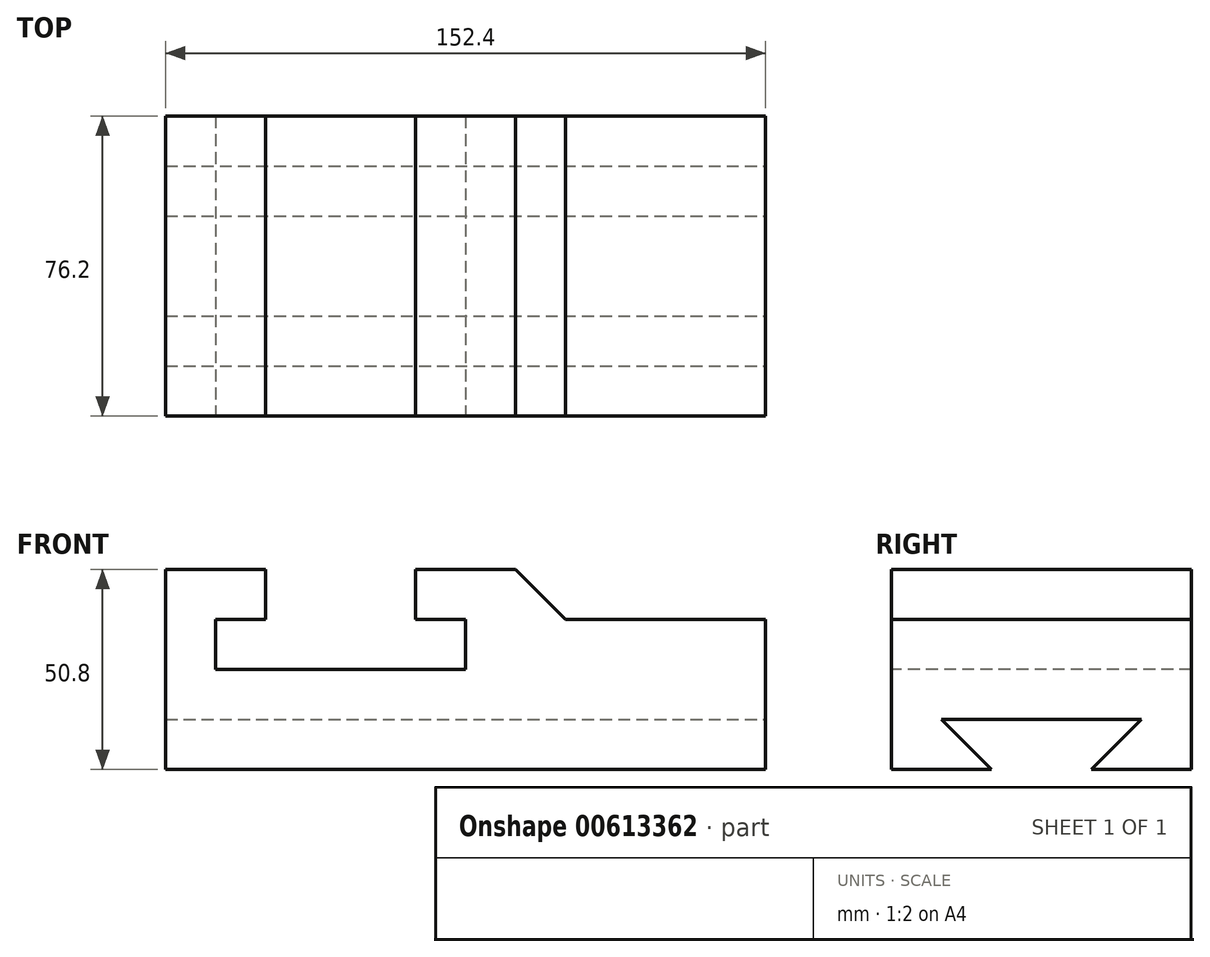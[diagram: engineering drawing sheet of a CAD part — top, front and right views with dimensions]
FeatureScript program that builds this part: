
annotation { "Feature Type Name" : "Feature", "Feature Type Description" : "" }
export const myFeature = defineFeature(function(context is Context, id is Id, definition is map)
    precondition{}
    {
        {
            var Q0;
            Q0=qCreatedBy(makeId("Front.planeOp"),FACE);
            var sketch = newSketch(context, id + "F0", { "sketchPlane" : qUnion([Q0])});
            skLineSegment(sketch, "E0", {"start": v(0, 0) * mm, "end": v(0, -50.8) * mm});
            skLineSegment(sketch, "E1", {"start": v(0, 0) * mm, "end": v(152.4, 0) * mm});
            skLineSegment(sketch, "E2", {"start": v(0, -50.8) * mm, "end": v(152.4, -50.8) * mm});
            skLineSegment(sketch, "E3", {"start": v(152.4, -50.8) * mm, "end": v(152.4, 0) * mm});
            skSolve(sketch);
        }
        {
            var Q0;
            Q0 = qSketchRegion(id + "F0", true);
            extrude(context, id + "F1", {"entities" : qUnion([Q0]), "depth" : 76.2 * mm, "offsetDistance" : 25.4 * mm});
        }
        {
            var Q0;
            Q0=makeQuery(id+"F1.opExtrude","CAP_FACE",FACE,{"disambiguationData":[OSD([sQuery(id+"F0.wireOp",EDGE,"E0"),sQuery(id+"F0.wireOp",EDGE,"E1"),sQuery(id+"F0.wireOp",EDGE,"E2"),sQuery(id+"F0.wireOp",EDGE,"E3")])],"isStart":false});
            var sketch = newSketch(context, id + "F2", { "sketchPlane" : qUnion([Q0])});
            skLineSegment(sketch, "E4", {"start": v(152.4, 0) * mm, "end": v(88.9, 0) * mm});
            skLineSegment(sketch, "E5", {"start": v(152.4, -12.7) * mm, "end": v(152.4, 0) * mm});
            skLineSegment(sketch, "E6", {"start": v(88.9, 0) * mm, "end": v(101.6, -12.7) * mm});
            skLineSegment(sketch, "E7", {"start": v(101.6, -12.7) * mm, "end": v(152.4, -12.7) * mm});
            skSolve(sketch);
        }
        {
            var Q0;
            Q0 = qSketchRegion(id + "F2", true);
            extrude(context, id + "F3", {"entities" : qUnion([Q0]), "operationType" : NewBodyOperationType.REMOVE, "oppositeDirection" : true, "depth" : 76.2 * mm, "offsetDistance" : 25.4 * mm});
        }
        {
            var Q0;
            Q0=makeQuery(id+"F1.opExtrude","CAP_FACE",FACE,{"disambiguationData":[OSD([sQuery(id+"F0.wireOp",EDGE,"E0"),sQuery(id+"F0.wireOp",EDGE,"E1"),sQuery(id+"F0.wireOp",EDGE,"E2"),sQuery(id+"F0.wireOp",EDGE,"E3")])],"isStart":false});
            var sketch = newSketch(context, id + "F4", { "sketchPlane" : qUnion([Q0])});
            skLineSegment(sketch, "E8", {"start": v(25.4, 0) * mm, "end": v(25.4, -12.7) * mm});
            skLineSegment(sketch, "E9", {"start": v(63.5, 0) * mm, "end": v(63.5, -12.7) * mm});
            skLineSegment(sketch, "E10", {"start": v(25.4, -12.7) * mm, "end": v(12.7, -12.7) * mm});
            skLineSegment(sketch, "E11", {"start": v(63.5, -12.7) * mm, "end": v(76.2, -12.7) * mm});
            skLineSegment(sketch, "E12", {"start": v(12.7, -12.7) * mm, "end": v(12.7, -25.4) * mm});
            skLineSegment(sketch, "E13", {"start": v(76.2, -12.7) * mm, "end": v(76.2, -25.4) * mm});
            skLineSegment(sketch, "E14", {"start": v(12.7, -25.4) * mm, "end": v(76.2, -25.4) * mm});
            skLineSegment(sketch, "E15", {"start": v(25.4, 0) * mm, "end": v(63.5, 0) * mm});
            skSolve(sketch);
        }
        {
            var Q0;
            Q0 = qSketchRegion(id + "F4", true);
            extrude(context, id + "F5", {"entities" : qUnion([Q0]), "operationType" : NewBodyOperationType.REMOVE, "oppositeDirection" : true, "depth" : 76.2 * mm, "offsetDistance" : 25.4 * mm});
        }
        {
            var Q0;
            Q0=makeQuery(id+"F1.opExtrude","SWEPT_FACE",FACE,{"disambiguationData":[OSD([sQuery(id+"F0.wireOp",EDGE,"E3")])]});
            var sketch = newSketch(context, id + "F6", { "sketchPlane" : qUnion([Q0])});
            skLineSegment(sketch, "E16", {"start": v(-50.8, -50.8) * mm, "end": v(-25.4, -50.8) * mm});
            skLineSegment(sketch, "E17", {"start": v(-50.8, -38.1) * mm, "end": v(-25.4, -38.1) * mm});
            skLineSegment(sketch, "E18", {"start": v(-25.4, -38.1) * mm, "end": v(-12.7, -38.1) * mm});
            skLineSegment(sketch, "E19", {"start": v(-50.8, -38.1) * mm, "end": v(-63.5, -38.1) * mm});
            skLineSegment(sketch, "E20", {"start": v(-63.5, -38.1) * mm, "end": v(-50.8, -50.8) * mm});
            skLineSegment(sketch, "E21", {"start": v(-12.7, -38.1) * mm, "end": v(-25.4, -50.8) * mm});
            skSolve(sketch);
        }
        {
            var Q0;
            Q0 = qSketchRegion(id + "F6", true);
            extrude(context, id + "F7", {"entities" : qUnion([Q0]), "operationType" : NewBodyOperationType.REMOVE, "oppositeDirection" : true, "depth" : 152.4 * mm, "offsetDistance" : 25.4 * mm});
        }
    });
